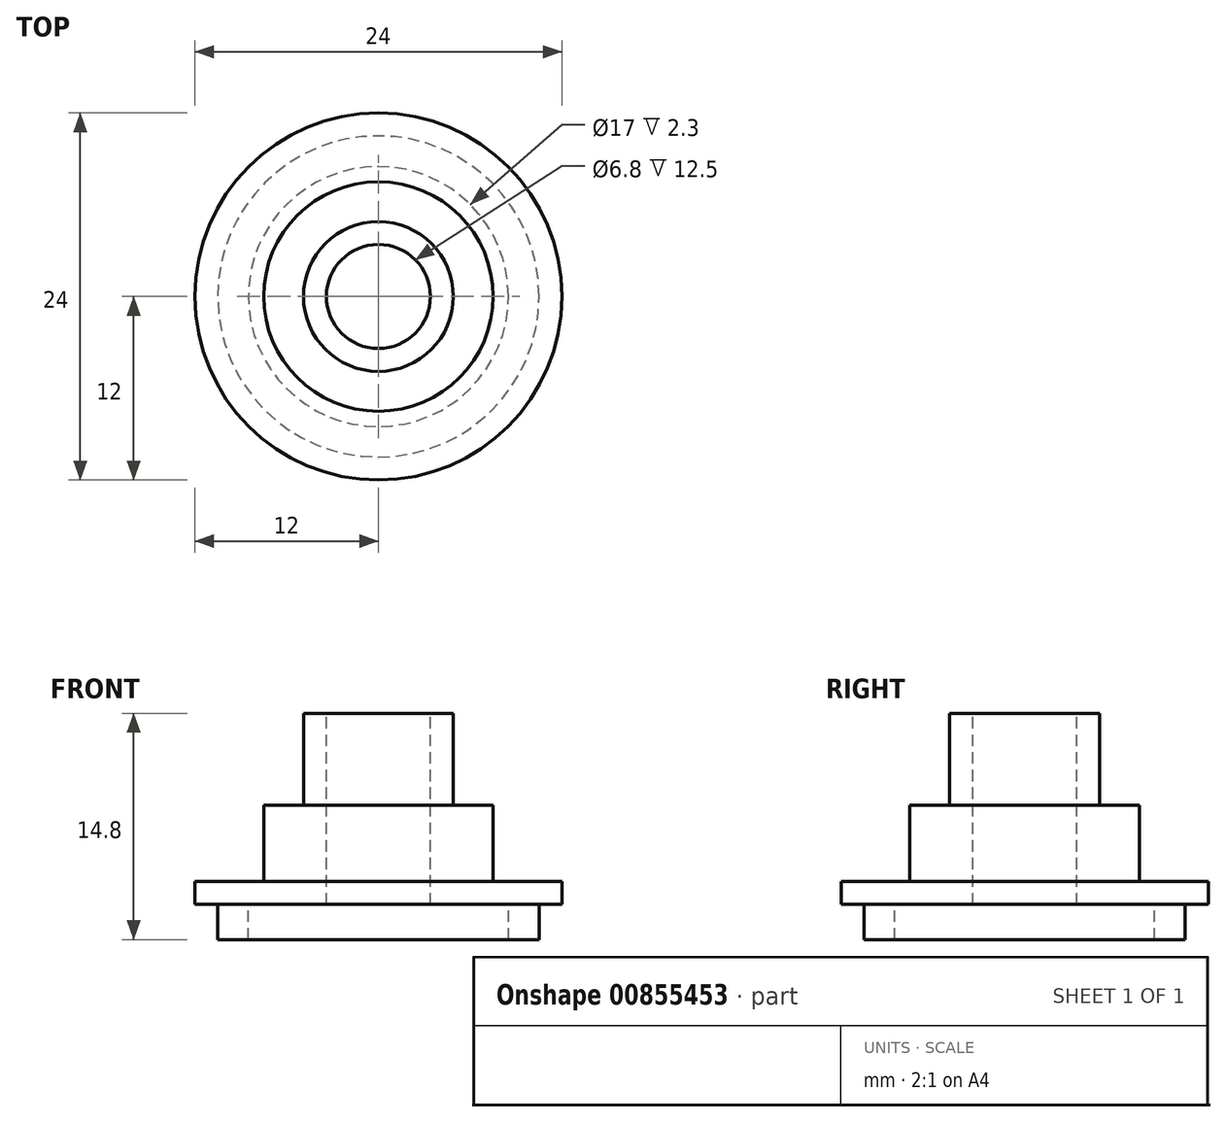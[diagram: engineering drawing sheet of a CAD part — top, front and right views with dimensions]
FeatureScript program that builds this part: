
annotation { "Feature Type Name" : "Feature", "Feature Type Description" : "" }
export const myFeature = defineFeature(function(context is Context, id is Id, definition is map)
    precondition{}
    {
        {
            var Q0;
            Q0=qCreatedBy(makeId("Right.planeOp"),FACE);
            var sketch = newSketch(context, id + "F0", { "sketchPlane" : qUnion([Q0])});
            skLineSegment(sketch, "E0", {"start": v(0, 0) * mm, "end": v(8.5, 0) * mm});
            skLineSegment(sketch, "E1", {"start": v(8.5, 0) * mm, "end": v(8.5, -2.3) * mm});
            skLineSegment(sketch, "E2", {"start": v(8.5, -2.3) * mm, "end": v(10.5, -2.3) * mm});
            skLineSegment(sketch, "E3", {"start": v(10.5, -2.3) * mm, "end": v(10.5, 0) * mm});
            skLineSegment(sketch, "E4", {"start": v(10.5, 0) * mm, "end": v(12, 0) * mm});
            skLineSegment(sketch, "E5", {"start": v(12, 0) * mm, "end": v(12, 1.5) * mm});
            skLineSegment(sketch, "E6", {"start": v(12, 1.5) * mm, "end": v(7.5, 1.5) * mm});
            skLineSegment(sketch, "E7", {"start": v(7.5, 1.5) * mm, "end": v(7.5, 6.5) * mm});
            skLineSegment(sketch, "E8", {"start": v(7.5, 6.5) * mm, "end": v(0, 6.5) * mm});
            skLineSegment(sketch, "E9", {"start": v(0, 6.5) * mm, "end": v(0, 0) * mm});
            skSolve(sketch);
        }
        {
            var Q0;
            Q0=qSketchRegion(id+"F0",true);
            var Q1;
            Q1=sQuery(id+"F0.wireOp",EDGE,"E9");
            revolve(context, id + "F1", {"surfaceOperationType" : NewSurfaceOperationType.NEW, "entities" : qUnion([Q0]), "axis" : qUnion([Q1]), "revolveType" : RevolveType.FULL});
        }
        {
            var Q0;
            Q0=makeQuery(id+"F1.opRevolve","SWEPT_FACE",FACE,{"disambiguationData":[OSD([sQuery(id+"F0.wireOp",EDGE,"E8")])]});
            var sketch = newSketch(context, id + "F2", { "sketchPlane" : qUnion([Q0])});
            skCircle(sketch, "E10", {"center": v(0, 0) * mm, "radius": 4.9 * mm});
            skSolve(sketch);
        }
        {
            var Q0;
            Q0=makeQuery(id+"F2.imprint","IMPRINT",FACE,{"disambiguationData":[TD([[makeQuery(id+"F2.imprint","IMPRINT",EDGE,{"derivedFrom":sQuery(id+"F2.wireOp",EDGE,"E10")}),1.0]])]});
            extrude(context, id + "F3", {"entities" : qUnion([Q0]), "operationType" : NewBodyOperationType.ADD, "depth" : 6 * mm, "offsetDistance" : 25 * mm});
        }
        {
            var Q0;
            Q0=makeQuery(id+"F3.opExtrude","CAP_FACE",FACE,{"disambiguationData":[OSD([sQuery(id+"F2.wireOp",EDGE,"E10")])],"isStart":false});
            var sketch = newSketch(context, id + "F4", { "sketchPlane" : qUnion([Q0])});
            skCircle(sketch, "E11", {"center": v(0, 0) * mm, "radius": 3.4 * mm});
            skSolve(sketch);
        }
        {
            var Q0;
            Q0=qSketchRegion(id+"F4",true);
            extrude(context, id + "F5", {"entities" : qUnion([Q0]), "operationType" : NewBodyOperationType.REMOVE, "endBound" : BoundingType.THROUGH_ALL, "oppositeDirection" : true, "depth" : 25 * mm, "offsetDistance" : 25 * mm});
        }
    });
